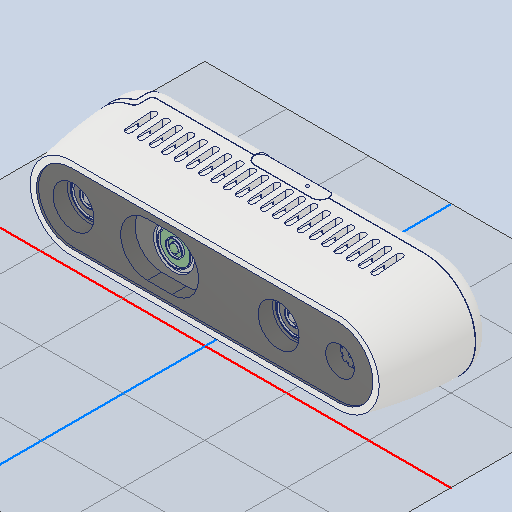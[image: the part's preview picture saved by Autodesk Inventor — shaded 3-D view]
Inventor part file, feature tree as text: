
AUTODESK INVENTOR PART (.ipt)
format: ipt  version: 2022 (Build 260153000, 153)  size: 1,157,632 bytes
history: imported  units: mm
features: other x9, projected_geometry x5, sketch x2, imported_body x1
ambient origin geometry x8: Origin, YZ Plane, XZ Plane, XY Plane, X Axis, Y Axis, Z Axis, Center Point
bodies: Solid1 (imported_parasolid), Solid2 (imported_parasolid), Solid3 (imported_parasolid), Solid4 (imported_parasolid), Solid5 (imported_parasolid), Solid6 (imported_parasolid), Solid7 (imported_parasolid), Solid8 (imported_parasolid)
feature tree (17):
  sketch  "Sketch1"
  other  "РабПлоскость1"
  sketch  "Эскиз2"
  projected_geometry  "Projected Loop1"
  projected_geometry  "Projected Loop2"
  projected_geometry  "Projected Loop3"
  projected_geometry  "Спроецированная петля4"
  projected_geometry  "Спроецированная петля5"
  other  "Cut-Extrude-Thin2[2]"
  other  "LPattern6[1]"
  other  "LPattern6[2]"
  other  "LPattern6[3]"
  other  "LPattern6[4]"
  other  "LPattern6[5]"
  other  "Dome2"
  other  "Boss-Extrude6"
  imported_body  NMx_Import_Brep_tag  [imported B-rep: ~17 faces, bbox_mm=None]
